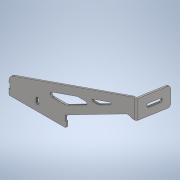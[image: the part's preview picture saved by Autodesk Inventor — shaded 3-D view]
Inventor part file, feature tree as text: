
AUTODESK INVENTOR PART (.ipt)
format: ipt  version: 2020 (Build 240168000, 168)  size: 437,760 bytes
history: native  units: mm
features: other x3, extrude x1, plane x1
ambient origin geometry x8: Origin, YZ Plane, XZ Plane, XY Plane, X Axis, Y Axis, Z Axis, Center Point
bodies: Body1 (feature_tree)
feature tree (5):
  other  "實體1"
  extrude  "擠出1"  Depth=130.0mm
  other  "折彎零件1"
  plane  "工作平面1"
  other  "定義1"
